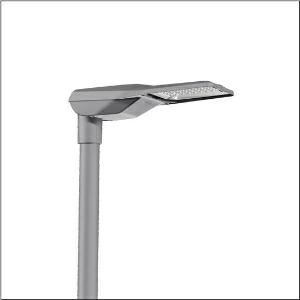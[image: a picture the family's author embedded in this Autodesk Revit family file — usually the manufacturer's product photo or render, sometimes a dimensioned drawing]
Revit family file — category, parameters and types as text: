
# Revit family: streetlight_sl_21_iq_mini___stw1_0a_5xe2e41d08gb_3fc6
name_source: partatom
category: Lighting Fixtures
units: mm (PartAtom-declared; Revit-internal decimal feet)

## family parameters
Cut with Voids When Loaded = No
Host = Face
Light Source = No
Part Type = Normal
Room Calculation Point = No
Round Connector Dimension = Use Diameter
Shared = No

## types (1)
- --- (1 x LED, 5920 lm, 37.1 W, 4000K)
    Apparent Load = 37 VA
    CIE Flux Codes = 38 75 98 100 100
    Color Rendering = 70
    Color Temperature = 4000K
    Default Elevation = 1800 mm
    Description = Streetlight SL 21 iQ mini, mast luminaire, primary light control with lens, of PMMA, primary optical cover: cover, of toughened safety glass, transparent, light distribution: STW1.0a, light emission: direct distribution, primary light characteristic: asymmetric, installation type: post-top, side-entry, LED, High Power LED, rated luminous flux: 5.920lm, luminous efficacy: 160lm/W, light colour: 740, colour temperature: 4000K, control: Auto-Match, Temp-Guard, Lumen-Switch, Night-Set, Smart-Wire, Light-Fading, Desk-Remote (wireless, voltage-free reading and setting of iQ features in the workshop via application-optimized NFC function/RFID function), optimised constant luminous flux control (CLO 2.0), presetting dimming linear, mains connection: 220..240V, AC, 50/60Hz, start of lifetime: 37W, end of service life: 39W, reduction: 18W, luminaire housing, of diecast aluminium, powder-coated, Siteco® metallic grey (DB 702S), corrosivity category C5 mid according to DIN EN ISO 12944, please order mast flange separately, inclination adjustable: 0°, 5°, 10°, 15°, sealing non-destructively replaceable, multi-level sealing system, length: 628mm, width: 235mm, height: 110mm, mast flange for spigot size: 42mm (side-entry): 5XC10008XM4, 60/48mm (side-entry/post-top): 5XC10108XM2, 76/60mm (side-entry/post-top): 5XC10108XM1, protection rating (complete): IP66, insulation class (complete): insulation class II (safety insulation), certification: CE, ENEC, ENEC+, VDE, impact resistance: IK09, permissible operating ambient temperature for outdoor applications: -40..+50°C, standard-compliant lighting for roads and squares, packaging unit: 1 piece

Light Distribution: STW1.0a
    Height = 110 mm
    Lamp = 1 x LED
    Lamp Light Flux = 5920 lm
    Lamp Power = 37.1 W
    Lamp count = 1
    Length = 625 mm
    Luminous efficacy = 160 lm/W
    Manufacturer = Siteco
    ModVariant = No
    Model = 5XE2E41D08GB
    Number of Poles = 1
    OnlyDefault = Yes
    Power Factor = 1
    Product Name = Streetlight SL 21 iQ mini | STW1.0a
    Product group = mast luminaire | pylon top
    ProductGroupID = 6100
    Protection Class = Protection class II
    Protection Degree = IP 66
    RLX_Detail_Level = 1
    RLX_Emergency_Light_Flux = 0 lm
    RLX_Emergency_Type = 0
    RLX_Emergency_Type_DB = No
    RlxData = <blob elided: 92025 chars, md5=736a4f9f>
    Socket = socket
    Standby Power = 0 W
    System Light Flux = 5920 lm
    System Power = 37 W
    Type Comments = factory setting: luminous flux: 100 % | dim-lin: 254 | 385 mA
    Type Image = l_1003519.jpg
    URL = http://relux.com
    VarID = @adj_139351
    Voltage = 0 V
    Weight = 0.00 kg
    Width = 234 mm

## geometry (parser evidence)
native form markers: Blend x4, Sweep x9
no freeform markers — native parametric forms only
